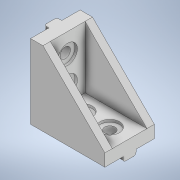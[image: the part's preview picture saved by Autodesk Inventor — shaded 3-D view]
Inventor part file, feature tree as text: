
AUTODESK INVENTOR PART (.ipt)
format: ipt  version: 2021 (Build 250183000, 183)  size: 240,128 bytes
history: native  units: mm
features: extrude x7, sketch x6, projected_geometry x4, other x3, mirror x3, fillet x1
ambient origin geometry x8: Origin, YZ Plane, XZ Plane, XY Plane, X Axis, Y Axis, Z Axis, Center Point
bodies: Body1 (feature_tree)
feature tree (24):
  other  "솔리드1"
  extrude  "돌출1"  Depth=30.0mm
  extrude  "돌출2"  Depth=5.0mm
  other  "작업 평면1"
  mirror  "미러1"
  extrude  "돌출3"  Depth=20.0mm TaperAngle=0.0deg
  fillet  "모깎기1"  Radius=5.2mm
  sketch  "스케치4"
  extrude  "돌출4"  Depth=2.0mm TaperAngle=0.0deg
  extrude  "돌출5"  Depth=2.0mm TaperAngle=0.0deg
  other  "작업 평면2"
  extrude  "돌출6"  Depth=1.0mm
  mirror  "미러2"
  extrude  "돌출7"  Depth=7.0mm
  mirror  "미러3"
  sketch  "스케치1"
  sketch  "스케치2"
  projected_geometry  "투영된 루프1"
  sketch  "스케치3"
  projected_geometry  "투영된 루프2"
  sketch  "스케치5"
  projected_geometry  "투영된 루프3"
  sketch  "스케치6"
  projected_geometry  "투영된 루프4"
